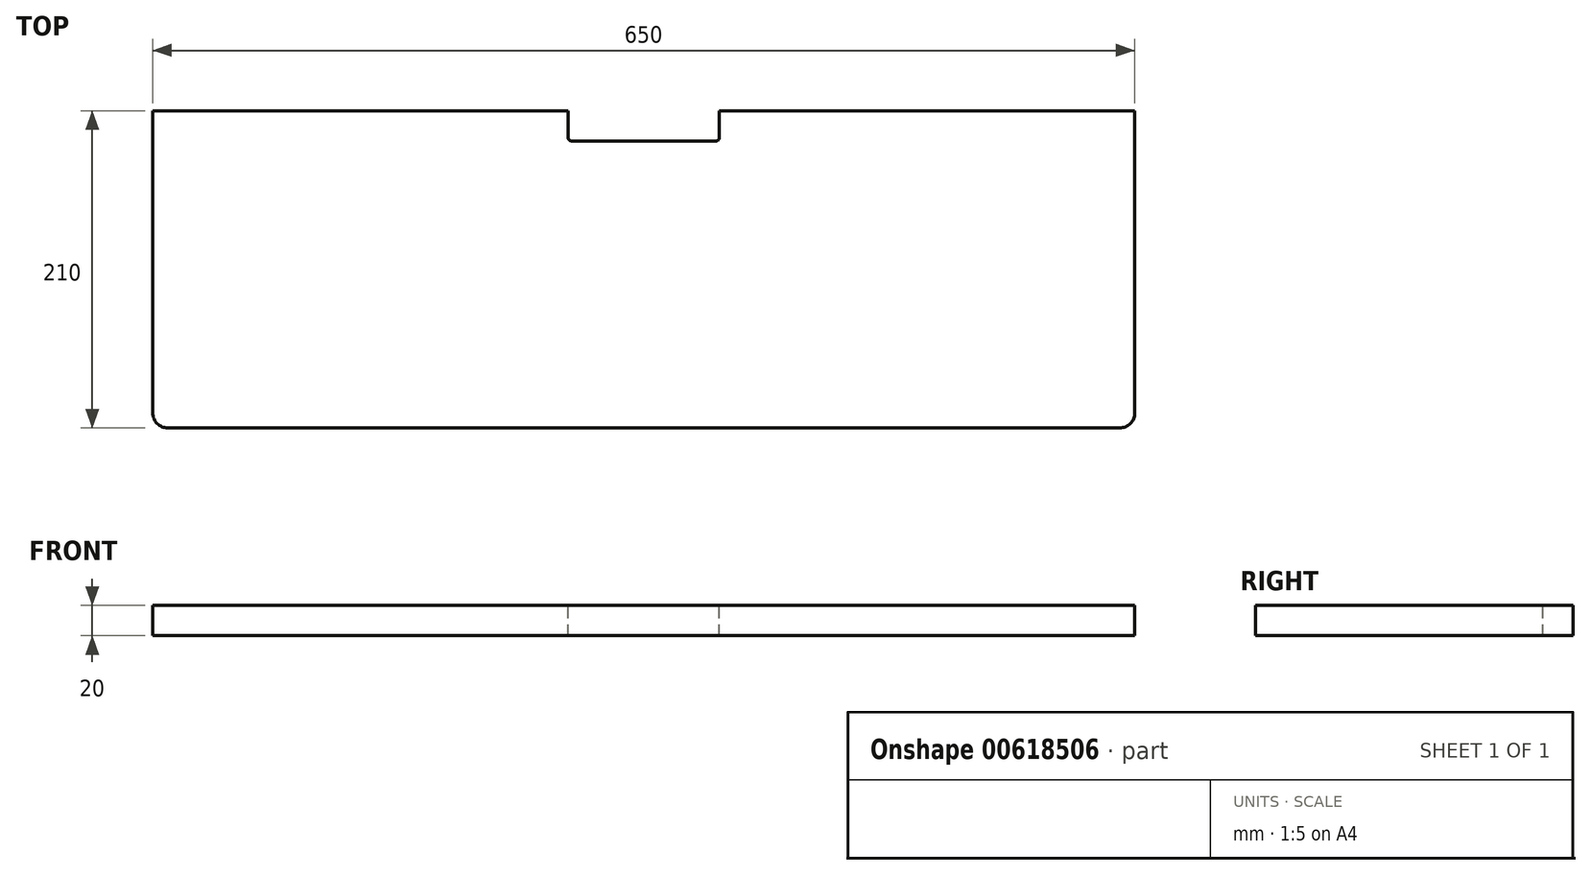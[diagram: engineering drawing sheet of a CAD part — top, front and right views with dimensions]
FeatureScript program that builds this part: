
annotation { "Feature Type Name" : "Feature", "Feature Type Description" : "" }
export const myFeature = defineFeature(function(context is Context, id is Id, definition is map)
    precondition{}
    {
        {
            var Q0;
            Q0=qCreatedBy(makeId("Top.planeOp"),FACE);
            var sketch = newSketch(context, id + "F0", { "sketchPlane" : qUnion([Q0])});
            skLineSegment(sketch, "E0.bottom", {"start": v(325, 105) * mm, "end": v(-325, 105) * mm});
            skLineSegment(sketch, "E0.top", {"start": v(325, -105) * mm, "end": v(-325, -105) * mm});
            skLineSegment(sketch, "E0.left", {"start": v(325, 105) * mm, "end": v(325, -105) * mm});
            skLineSegment(sketch, "E0.right", {"start": v(-325, 105) * mm, "end": v(-325, -105) * mm});
            skPoint(sketch, "E0.middle", {"position": v(0, 0) * mm});
            skSolve(sketch);
        }
        {
            var Q0;
            Q0=makeQuery(id+"F0.imprint","IMPRINT",FACE,{"disambiguationData":[TD([[makeQuery(id+"F0.imprint","IMPRINT",EDGE,{"derivedFrom":sQuery(id+"F0.wireOp",EDGE,"E0.bottom")}),1.0]])]});
            extrude(context, id + "F1", {"entities" : qUnion([Q0]), "depth" : 20 * mm, "offsetDistance" : 25 * mm});
        }
        {
            var Q0;
            Q0=makeQuery(id+"F1.opExtrude","CAP_FACE",FACE,{"disambiguationData":[OSD([sQuery(id+"F0.wireOp",EDGE,"E0.bottom"),sQuery(id+"F0.wireOp",EDGE,"E0.top"),sQuery(id+"F0.wireOp",EDGE,"E0.left"),sQuery(id+"F0.wireOp",EDGE,"E0.right")])],"isStart":false});
            var sketch = newSketch(context, id + "F2", { "sketchPlane" : qUnion([Q0])});
            skLineSegment(sketch, "E1.bottom", {"start": v(50, 105) * mm, "end": v(-50, 105) * mm});
            skLineSegment(sketch, "E1.top", {"start": v(50, 85) * mm, "end": v(-50, 85) * mm});
            skLineSegment(sketch, "E1.left", {"start": v(50, 105) * mm, "end": v(50, 85) * mm});
            skLineSegment(sketch, "E1.right", {"start": v(-50, 105) * mm, "end": v(-50, 85) * mm});
            skPoint(sketch, "E1.middle", {"position": v(0, 95) * mm});
            skSolve(sketch);
        }
        {
            var Q0;
            Q0=makeQuery(id+"F2.imprint","IMPRINT",FACE,{"disambiguationData":[TD([[makeQuery(id+"F2.imprint","IMPRINT",EDGE,{"derivedFrom":sQuery(id+"F2.wireOp",EDGE,"E1.bottom")}),1.0]])]});
            extrude(context, id + "F3", {"entities" : qUnion([Q0]), "operationType" : NewBodyOperationType.REMOVE, "endBound" : BoundingType.THROUGH_ALL, "oppositeDirection" : true, "depth" : 25 * mm, "offsetDistance" : 25 * mm});
        }
        {
            var Q0;
            Q0=makeQuery(id+"F1.opExtrude","SWEPT_EDGE",EDGE,{"disambiguationData":[OSD([sQuery(id+"F0.wireOp",EDGE,"E0.top"),sQuery(id+"F0.wireOp",EDGE,"E0.right")])]});
            var Q1;
            Q1=makeQuery(id+"F1.opExtrude","SWEPT_EDGE",EDGE,{"disambiguationData":[OSD([sQuery(id+"F0.wireOp",EDGE,"E0.top"),sQuery(id+"F0.wireOp",EDGE,"E0.left")])]});
            fillet(context, id + "F4", {"entities" : qUnion([Q0, Q1]), "radius" : 10 * mm, "tangentPropagation" : true, "allowEdgeOverflow" : false});
        }
        {
            var Q0;
            Q0=makeQuery(id+"F3.boolean.opBoolean","COPY",EDGE,{"derivedFrom":makeQuery(id+"F3.opExtrude","SWEPT_EDGE",EDGE,{"disambiguationData":[OSD([sQuery(id+"F2.wireOp",EDGE,"E1.top"),sQuery(id+"F2.wireOp",EDGE,"E1.right")])]})});
            var Q1;
            Q1=makeQuery(id+"F3.boolean.opBoolean","COPY",EDGE,{"derivedFrom":makeQuery(id+"F3.opExtrude","SWEPT_EDGE",EDGE,{"disambiguationData":[OSD([sQuery(id+"F2.wireOp",EDGE,"E1.top"),sQuery(id+"F2.wireOp",EDGE,"E1.left")])]})});
            fillet(context, id + "F5", {"entities" : qUnion([Q0, Q1]), "radius" : 2 * mm, "tangentPropagation" : true, "allowEdgeOverflow" : false});
        }
    });
